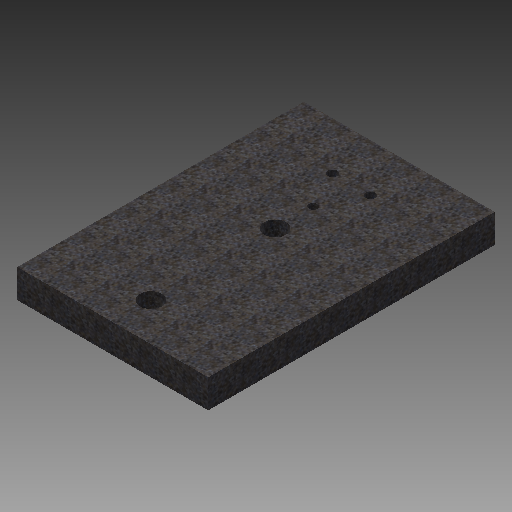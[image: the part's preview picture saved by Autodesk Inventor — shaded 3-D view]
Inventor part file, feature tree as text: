
AUTODESK INVENTOR PART (.ipt)
format: ipt  version: 2017 (Build 210142000, 142)  size: 269,312 bytes
history: native  units: in
note: dims shown in document units (in); Inventor stores cm internally (conversion verified against a paired STEP export)
features: sketch x5, extrude x3, hole x2
ambient origin geometry x8: Origin, YZ Plane, XZ Plane, XY Plane, X Axis, Y Axis, Z Axis, Center Point
bodies: Solid1 (feature_tree)
feature tree (10):
  extrude  "base"  Depth=59.0551in
  extrude  "air"  Depth=5.9055in
  extrude  "power"  Depth=1.9291in
  hole  "fibre"  [1 undecoded]
  hole  "air2"  [1 undecoded]
  sketch  "Sketch1"  dims[d0=39.3701in d1=59.0551in]
  sketch  "Sketch2"  dims[d2=5.9055in d3=0.0in d4=4.5276in]
  sketch  "Sketch3"  dims[d5=1.0in d6=0.0in d7=1.9291in]
  sketch  "Sketch4"  dims[d9=10.0in d10=0.0in]
  sketch  "Sketch6"  dims[d13=1.7717in d14=0.75in d15=0.375in d16=0.25in d17=0.5635in d18=1.0in d19=0.8108in d29=6.0in d30=25.5906in d31=4.5276in d32=0.75in d33=0.375in d34=0.25in d35=0.5635in d36=1.0in d37=0.8108in d38=25.5906in d40=3.937in d41=1.9291in d42=3.937in d52=1.9291in d53=17.7165in d55=9.8425in]
note: 2 required parameter values undecoded (feature->parameter linkage not recoverable at this tier; creation-order binding heuristic only, values carry confidence <= 0.55)
